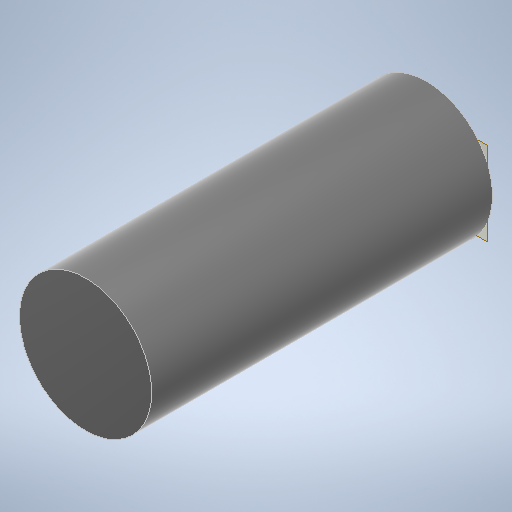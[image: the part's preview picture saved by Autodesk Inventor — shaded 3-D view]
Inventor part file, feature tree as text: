
AUTODESK INVENTOR PART (.ipt)
format: ipt  version: 2025.1 (Build 291241020, 241B)  size: 596,992 bytes
history: native  units: mm
features: extrude x8, sketch x8, plane x1, mirror x1
ambient origin geometry x8: Origin, YZ Plane, XZ Plane, XY Plane, X Axis, Y Axis, Z Axis, Center Point
bodies: Solid1 (feature_tree)
feature tree (18):
  extrude  "Extrusion1"  Depth=39.0mm
  plane  "Work Plane1"
  extrude  "Extrusion2"  Depth=3.0mm TaperAngle=0.0deg
  mirror  "Mirror1"
  extrude  "Extrusion5"  Depth=10.0mm TaperAngle=0.0deg
  extrude  "Extrusion6"  Depth=7.0mm
  extrude  "Extrusion7"  Depth=20.4mm
  extrude  "Extrusion8"  TaperAngle=0.0deg  [1 undecoded]
  extrude  "Extrusion9"  Depth=0.9mm
  extrude  "Extrusion10"  [1 undecoded]
  sketch  "Sketch1"  dims[d0=33.0mm d1=39.0mm]
  sketch  "Sketch2"  dims[d2=195.0mm d3=0.0mm d4=3.0mm d5=0.0mm]
  sketch  "Sketch5"  dims[d12=22.0mm d13=10.0mm d14=0.0mm]
  sketch  "Sketch6"  dims[d15=0.0mm d16=0.0mm d17=7.0mm]
  sketch  "Sketch7"  dims[d18=0.0mm d19=0.0mm d20=20.4mm]
  sketch  "Sketch8"  dims[d21=5.0mm d22=0.0mm d23=0.0mm d24=0.0mm]
  sketch  "Sketch9"  dims[d25=33.0mm d26=0.9mm]
  sketch  "Sketch10"  dims[d27=3.1mm d28=0.0mm]
note: 2 required parameter values undecoded (feature->parameter linkage not recoverable at this tier; creation-order binding heuristic only, values carry confidence <= 0.55)
